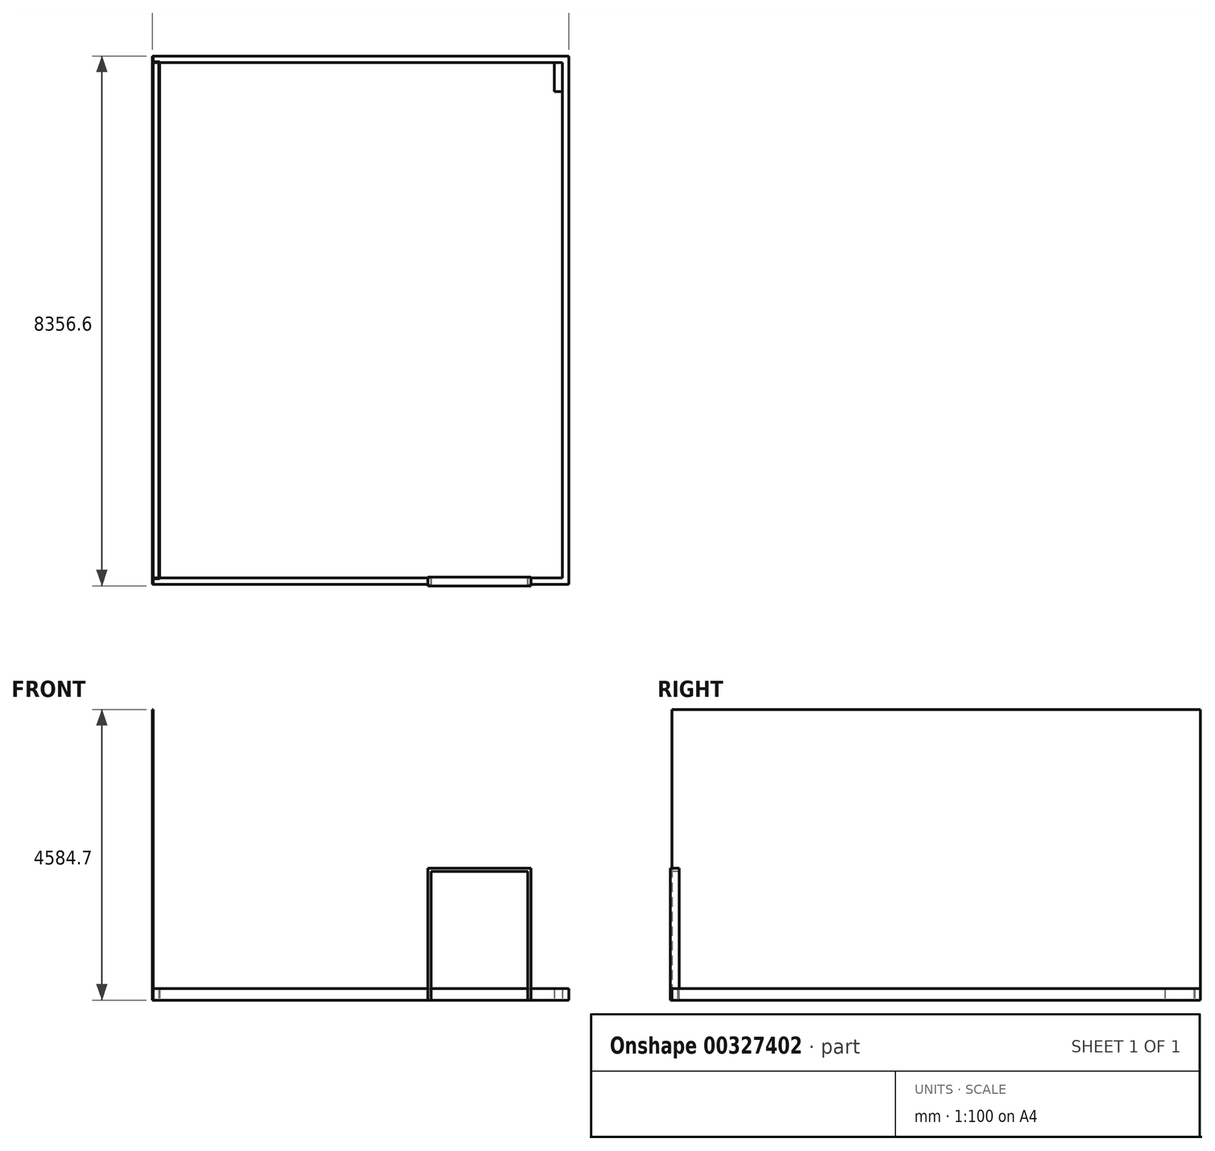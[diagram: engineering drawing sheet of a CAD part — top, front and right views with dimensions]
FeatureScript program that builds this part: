
annotation { "Feature Type Name" : "Feature", "Feature Type Description" : "" }
export const myFeature = defineFeature(function(context is Context, id is Id, definition is map)
    precondition{}
    {
        {
            assignVariable(context, id + "F0", {"name" : "WallHeight", "anyValue" : 15 * 12 + 0.5});
        }
        {
            var Q0;
            Q0=qCreatedBy(makeId("Top.planeOp"),FACE);
            var sketch = newSketch(context, id + "F1", { "sketchPlane" : qUnion([Q0])});
            skLineSegment(sketch, "E0.bottom", {"start": v(0, 8128) * mm, "end": v(6350, 8128) * mm});
            skLineSegment(sketch, "E0.top", {"start": v(0, 0) * mm, "end": v(6350, 0) * mm});
            skLineSegment(sketch, "E0.left", {"start": v(0, 8128) * mm, "end": v(0, 0) * mm});
            skLineSegment(sketch, "E0.right", {"start": v(6350, 8128) * mm, "end": v(6350, 0) * mm});
            skSolve(sketch);
        }
        {
            var Q0;
            Q0=qCreatedBy(makeId("Top.planeOp"),FACE);
            var sketch = newSketch(context, id + "F2", { "sketchPlane" : qUnion([Q0])});
            skLineSegment(sketch, "E1.bottom", {"start": v(0, 0) * mm, "end": v(-12.7, 0) * mm});
            skLineSegment(sketch, "E1.top", {"start": v(0, 8128) * mm, "end": v(-12.7, 8128) * mm});
            skLineSegment(sketch, "E1.left", {"start": v(0, 0) * mm, "end": v(0, 8128) * mm});
            skLineSegment(sketch, "E1.right", {"start": v(-12.7, 0) * mm, "end": v(-12.7, 8128) * mm});
            skSolve(sketch);
        }
        {
            var Q0;
            Q0=makeQuery(id+"F2.imprint","IMPRINT",FACE,{"disambiguationData":[TD([[makeQuery(id+"F2.imprint","IMPRINT",EDGE,{"derivedFrom":sQuery(id+"F2.wireOp",EDGE,"E1.bottom")}),-1.0]])]});
            extrude(context, id + "F3", {"entities" : qUnion([Q0]), "depth" : (getVariable(context, 'WallHeight')) * mm});
        }
        {
            var Q0;
            Q0=qCreatedBy(makeId("Top.planeOp"),FACE);
            var sketch = newSketch(context, id + "F4", { "sketchPlane" : qUnion([Q0])});
            skLineSegment(sketch, "E2.bottom", {"start": v(0, 0) * mm, "end": v(6350, 0) * mm});
            skLineSegment(sketch, "E2.top", {"start": v(0, -12.7) * mm, "end": v(6350, -12.7) * mm});
            skLineSegment(sketch, "E2.left", {"start": v(0, 0) * mm, "end": v(0, -12.7) * mm});
            skLineSegment(sketch, "E2.right", {"start": v(6350, 0) * mm, "end": v(6350, -12.7) * mm});
            skSolve(sketch);
        }
        {
            var Q0;
            Q0 = qSketchRegion(id + "F4", true);
            extrude(context, id + "F5", {"entities" : qUnion([Q0]), "depth" : (getVariable(context, 'WallHeight')) * mm});
        }
        {
            var Q0;
            Q0=qCreatedBy(makeId("Top.planeOp"),FACE);
            var sketch = newSketch(context, id + "F6", { "sketchPlane" : qUnion([Q0])});
            skLineSegment(sketch, "E3.bottom", {"start": v(6350, 0) * mm, "end": v(6362.7, 0) * mm});
            skLineSegment(sketch, "E3.top", {"start": v(6350, 8128) * mm, "end": v(6362.7, 8128) * mm});
            skLineSegment(sketch, "E3.left", {"start": v(6350, 0) * mm, "end": v(6350, 8128) * mm});
            skLineSegment(sketch, "E3.right", {"start": v(6362.7, 0) * mm, "end": v(6362.7, 8128) * mm});
            skSolve(sketch);
        }
        {
            var Q0;
            Q0 = qSketchRegion(id + "F6", true);
            extrude(context, id + "F7", {"entities" : qUnion([Q0]), "depth" : (getVariable(context, 'WallHeight')) * mm});
        }
        {
            var Q0;
            Q0=qCreatedBy(makeId("Top.planeOp"),FACE);
            var sketch = newSketch(context, id + "F8", { "sketchPlane" : qUnion([Q0])});
            skLineSegment(sketch, "E4.bottom", {"start": v(0, 8128) * mm, "end": v(6350, 8128) * mm});
            skLineSegment(sketch, "E4.top", {"start": v(0, 8140.7) * mm, "end": v(6350, 8140.7) * mm});
            skLineSegment(sketch, "E4.left", {"start": v(0, 8128) * mm, "end": v(0, 8140.7) * mm});
            skLineSegment(sketch, "E4.right", {"start": v(6350, 8128) * mm, "end": v(6350, 8140.7) * mm});
            skSolve(sketch);
        }
        {
            var Q0;
            Q0 = qSketchRegion(id + "F8", true);
            extrude(context, id + "F9", {"entities" : qUnion([Q0]), "depth" : (getVariable(context, 'WallHeight')) * mm});
        }
        {
            var Q0;
            Q0=makeQuery(id+"F3.opExtrude","SWEPT_FACE",FACE,{"disambiguationData":[OSD([sQuery(id+"F2.wireOp",EDGE,"E1.right")])]});
            extrude(context, id + "F10", {"entities" : qUnion([Q0]), "depth" : 88.9 * mm});
        }
        {
            var Q0;
            Q0=makeQuery(id+"F7.opExtrude","SWEPT_FACE",FACE,{"disambiguationData":[OSD([sQuery(id+"F6.wireOp",EDGE,"E3.right")])]});
            extrude(context, id + "F11", {"entities" : qUnion([Q0]), "depth" : 88.9 * mm});
        }
        {
            var Q0;
            Q0=makeQuery(id+"F5.opExtrude","SWEPT_FACE",FACE,{"disambiguationData":[OSD([sQuery(id+"F4.wireOp",EDGE,"E2.top")])]});
            extrude(context, id + "F12", {"entities" : qUnion([Q0]), "depth" : 88.9 * mm});
        }
        {
            var Q0;
            Q0=makeQuery(id+"F12.opExtrude","SWEPT_FACE",FACE,{"disambiguationData":[OSD([sQuery(id+"F4.wireOp",EDGE,"E2.top"),sQuery(id+"F4.wireOp",EDGE,"E2.left")])]});
            extrude(context, id + "F13", {"entities" : qUnion([Q0]), "operationType" : NewBodyOperationType.ADD, "depth" : 101.6 * mm});
        }
        {
            var Q0;
            Q0=makeQuery(id+"F12.opExtrude","SWEPT_FACE",FACE,{"disambiguationData":[OSD([sQuery(id+"F4.wireOp",EDGE,"E2.top"),sQuery(id+"F4.wireOp",EDGE,"E2.right")])]});
            extrude(context, id + "F14", {"entities" : qUnion([Q0]), "operationType" : NewBodyOperationType.ADD, "depth" : 101.6 * mm});
        }
        {
            var Q0;
            Q0=makeQuery(id+"F9.opExtrude","SWEPT_FACE",FACE,{"disambiguationData":[OSD([sQuery(id+"F8.wireOp",EDGE,"E4.top")])]});
            extrude(context, id + "F15", {"entities" : qUnion([Q0]), "depth" : 88.9 * mm});
        }
        {
            var Q0;
            Q0=makeQuery(id+"F15.opExtrude","SWEPT_FACE",FACE,{"disambiguationData":[OSD([sQuery(id+"F8.wireOp",EDGE,"E4.top"),sQuery(id+"F8.wireOp",EDGE,"E4.left")])]});
            extrude(context, id + "F16", {"entities" : qUnion([Q0]), "operationType" : NewBodyOperationType.ADD, "depth" : 101.6 * mm});
        }
        {
            var Q0;
            Q0=makeQuery(id+"F15.opExtrude","SWEPT_FACE",FACE,{"disambiguationData":[OSD([sQuery(id+"F8.wireOp",EDGE,"E4.top"),sQuery(id+"F8.wireOp",EDGE,"E4.right")])]});
            extrude(context, id + "F17", {"entities" : qUnion([Q0]), "operationType" : NewBodyOperationType.ADD, "depth" : 101.6 * mm});
        }
        {
            var Q0;
            Q0=makeQuery(id+"F10.opExtrude","CAP_FACE",FACE,{"disambiguationData":[OSD([sQuery(id+"F2.wireOp",EDGE,"E1.right")])],"isStart":false});
            var sketch = newSketch(context, id + "F18", { "sketchPlane" : qUnion([Q0])});
            skLineSegment(sketch, "E5.bottom", {"start": v(-8229.6, 4584.7) * mm, "end": v(101.6, 4584.7) * mm});
            skLineSegment(sketch, "E5.top", {"start": v(-8229.6, 0) * mm, "end": v(101.6, 0) * mm});
            skLineSegment(sketch, "E5.left", {"start": v(-8229.6, 4584.7) * mm, "end": v(-8229.6, 0) * mm});
            skLineSegment(sketch, "E5.right", {"start": v(101.6, 4584.7) * mm, "end": v(101.6, 0) * mm});
            skSolve(sketch);
        }
        {
            var Q0;
            Q0 = qSketchRegion(id + "F18", true);
            extrude(context, id + "F19", {"entities" : qUnion([Q0]), "depth" : 12.7 * mm});
        }
        {
            var Q0;
            {var subQ0=sQuery(id+"F4.wireOp",EDGE,"E2.right");var subQ1=sQuery(id+"F4.wireOp",EDGE,"E2.top");var subQ2=sQuery(id+"F4.wireOp",EDGE,"E2.left");Q0=makeQuery(id+"F14.boolean.opBoolean","MERGE",FACE,{"derivedFrom":[makeQuery(id+"F13.boolean.opBoolean","MERGE",FACE,{"derivedFrom":[makeQuery(id+"F12.opExtrude","CAP_FACE",FACE,{"disambiguationData":[OSD([subQ1])],"isStart":false}),makeQuery(id+"F13.opExtrude","SWEPT_FACE",FACE,{"disambiguationData":[OSD([subQ1,subQ2]),TDD([makeQuery(id+"F12.opExtrude","CAP_EDGE",EDGE,{"disambiguationData":[OSD([subQ1,subQ2])],"isStart":false})])]})]}),makeQuery(id+"F14.opExtrude","SWEPT_FACE",FACE,{"disambiguationData":[OSD([subQ1,subQ0]),TDD([makeQuery(id+"F12.opExtrude","CAP_EDGE",EDGE,{"disambiguationData":[OSD([subQ1,subQ0])],"isStart":false})])]})]});}
            var sketch = newSketch(context, id + "F20", { "sketchPlane" : qUnion([Q0])});
            skLineSegment(sketch, "E6.bottom", {"start": v(4225.93, 0) * mm, "end": v(5851.53, 0) * mm});
            skLineSegment(sketch, "E6.top", {"start": v(4225.93, 2082.8) * mm, "end": v(5851.53, 2082.8) * mm});
            skLineSegment(sketch, "E6.left", {"start": v(4225.93, 0) * mm, "end": v(4225.93, 2082.8) * mm});
            skLineSegment(sketch, "E6.right", {"start": v(5851.53, 0) * mm, "end": v(5851.53, 2082.8) * mm});
            skSolve(sketch);
        }
        {
            var Q0;
            Q0 = qSketchRegion(id + "F20", true);
            extrude(context, id + "F21", {"entities" : qUnion([Q0]), "flatOperationType" : FlatOperationType.REMOVE, "offsetDistance" : 25.4 * mm, "depth" : 25.4 * mm, "hasSecondDirection" : true, "secondDirectionOppositeDirection" : true, "secondDirectionDepth" : 114.3 * mm, "domain" : OperationDomain.MODEL});
        }
        {
            var Q0;
            Q0=makeQuery(id+"F21.opExtrude","CAP_FACE",FACE,{"disambiguationData":[OSD([sQuery(id+"F20.wireOp",EDGE,"E6.bottom"),sQuery(id+"F20.wireOp",EDGE,"E6.top"),sQuery(id+"F20.wireOp",EDGE,"E6.left"),sQuery(id+"F20.wireOp",EDGE,"E6.right")])],"isStart":false});
            var sketch = newSketch(context, id + "F22", { "sketchPlane" : qUnion([Q0])});
            skLineSegment(sketch, "E7.bottom", {"start": v(4276.72, 0) * mm, "end": v(5800.73, 0) * mm});
            skLineSegment(sketch, "E7.top", {"start": v(4276.72, 2032) * mm, "end": v(5800.73, 2032) * mm});
            skLineSegment(sketch, "E7.left", {"start": v(4276.73, 0) * mm, "end": v(4276.73, 2032) * mm});
            skLineSegment(sketch, "E7.right", {"start": v(5800.73, 0) * mm, "end": v(5800.73, 2032) * mm});
            skSolve(sketch);
        }
        {
            var Q0;
            Q0 = qSketchRegion(id + "F22", true);
            var Q1;
            Q1=makeQuery(id+"F21.opExtrude","CAP_FACE",FACE,{"disambiguationData":[OSD([sQuery(id+"F20.wireOp",EDGE,"E6.bottom"),sQuery(id+"F20.wireOp",EDGE,"E6.top"),sQuery(id+"F20.wireOp",EDGE,"E6.left"),sQuery(id+"F20.wireOp",EDGE,"E6.right")])],"isStart":true});
            extrude(context, id + "F23", {"entities" : qUnion([Q0]), "operationType" : NewBodyOperationType.REMOVE, "endBound" : BoundingType.UP_TO_SURFACE, "oppositeDirection" : true, "endBoundEntityFace" : qUnion([Q1]), "offsetDistance" : 25.4 * mm, "depth" : 25.4 * mm});
        }
        {
            var Q0;
            Q0=makeQuery(id+"F1.imprint","IMPRINT",FACE,{"disambiguationData":[TD([[makeQuery(id+"F1.imprint","IMPRINT",EDGE,{"derivedFrom":sQuery(id+"F1.wireOp",EDGE,"E0.bottom")}),-1.0]])]});
            var sketch = newSketch(context, id + "F24", { "sketchPlane" : qUnion([Q0])});
            skLineSegment(sketch, "E8.bottom", {"start": v(6350, 8128) * mm, "end": v(6223, 8128) * mm});
            skLineSegment(sketch, "E8.top", {"start": v(6350, 7670.8) * mm, "end": v(6223, 7670.8) * mm});
            skLineSegment(sketch, "E8.left", {"start": v(6350, 8128) * mm, "end": v(6350, 7670.8) * mm});
            skLineSegment(sketch, "E8.right", {"start": v(6223, 8128) * mm, "end": v(6223, 7670.8) * mm});
            skSolve(sketch);
        }
        {
            var Q0;
            Q0 = qSketchRegion(id + "F24", true);
            var Q1;
            Q1=makeQuery(id+"F7.opExtrude","CAP_FACE",FACE,{"disambiguationData":[OSD([sQuery(id+"F6.wireOp",EDGE,"E3.bottom"),sQuery(id+"F6.wireOp",EDGE,"E3.top"),sQuery(id+"F6.wireOp",EDGE,"E3.left"),sQuery(id+"F6.wireOp",EDGE,"E3.right")])],"isStart":false});
            extrude(context, id + "F25", {"entities" : qUnion([Q0]), "endBound" : BoundingType.UP_TO_SURFACE, "depth" : 25.4 * mm, "endBoundEntityFace" : qUnion([Q1]), "offsetDistance" : 25.4 * mm});
        }
    });
